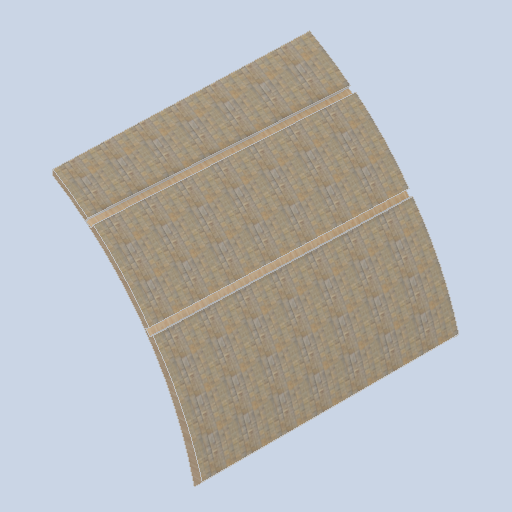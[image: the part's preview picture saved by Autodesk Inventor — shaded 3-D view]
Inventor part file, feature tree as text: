
AUTODESK INVENTOR PART (.ipt)
format: ipt  version: 2024.2 (Build 282272000, 272)  size: 356,352 bytes
history: native  units: in
note: dims shown in document units (in); Inventor stores cm internally (conversion verified against a paired STEP export)
features: other x3, sketch x2, plane x2
ambient origin geometry x8: Origin, YZ Plane, XZ Plane, XY Plane, X Axis, Y Axis, Z Axis, Center Point
bodies: Solid1 (feature_tree)
feature tree (7):
  other  "panel_block_03.ipt"
  other  "Solid1::panel_block_03.ipt"
  other  "TaggingFeature1"
  sketch  "Sketch1"  dims[d0=0.3937in]
  sketch  "Sketch2"
  plane  "Work Plane1"
  plane  "Work Plane2"
